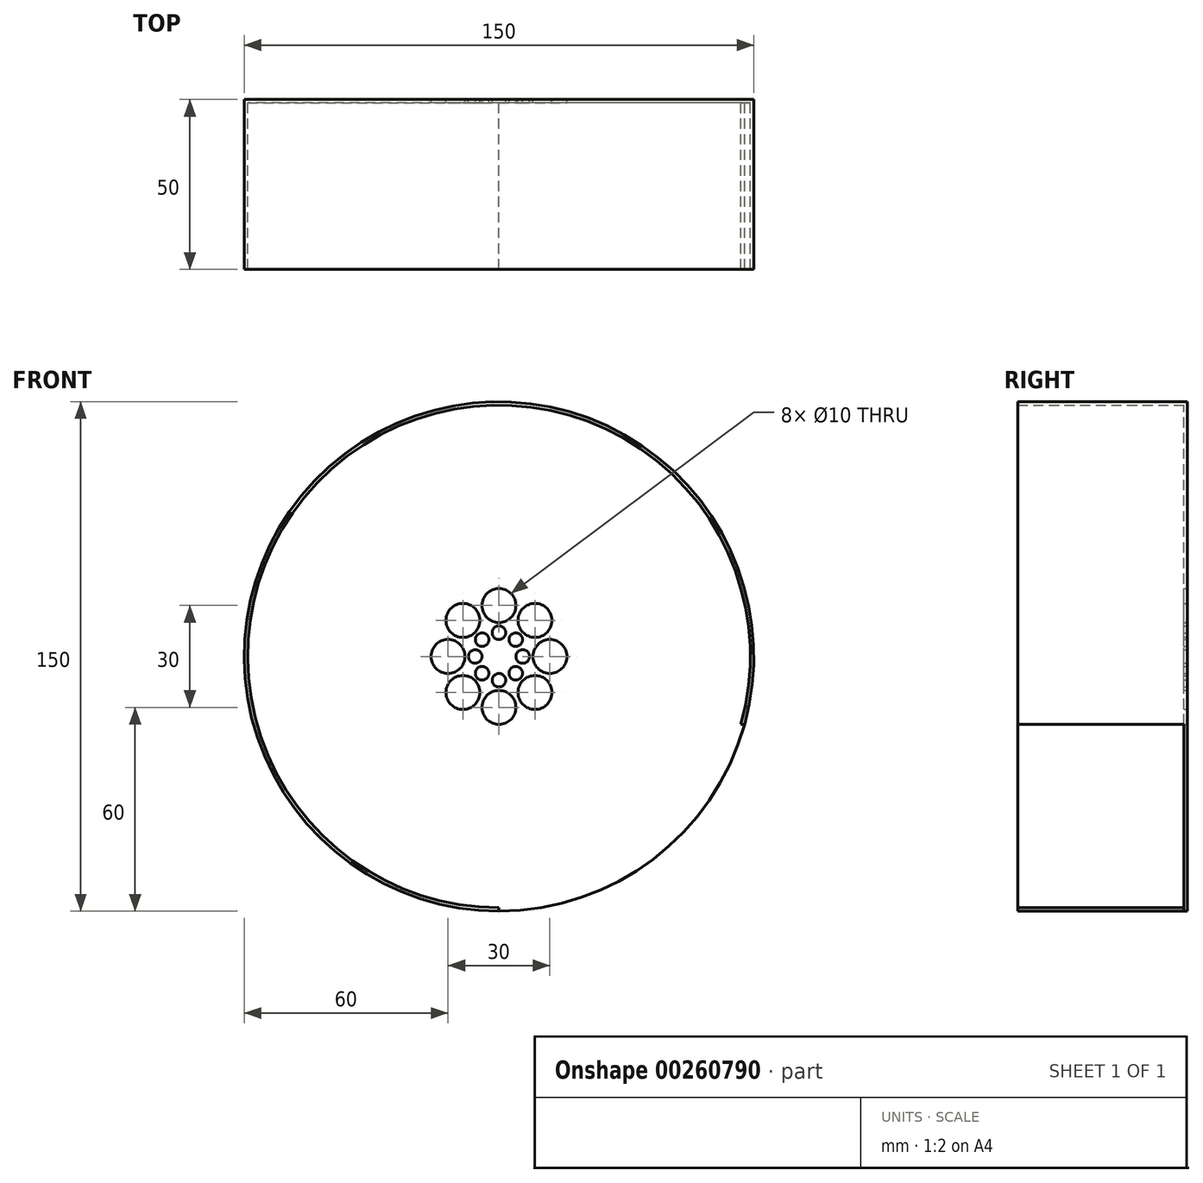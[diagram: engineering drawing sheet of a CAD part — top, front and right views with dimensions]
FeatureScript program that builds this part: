
annotation { "Feature Type Name" : "Feature", "Feature Type Description" : "" }
export const myFeature = defineFeature(function(context is Context, id is Id, definition is map)
    precondition{}
    {
        {
            var Q0;
            Q0=qCreatedBy(makeId("Front.planeOp"),FACE);
            var sketch = newSketch(context, id + "F0", { "sketchPlane" : qUnion([Q0])});
            skCircle(sketch, "E0", {"center": v(0, 0) * mm, "radius": 75 * mm});
            skSolve(sketch);
        }
        {
            var Q0;
            Q0=makeQuery(id+"F0.imprint","IMPRINT",FACE,{"disambiguationData":[TD([[makeQuery(id+"F0.imprint","IMPRINT",EDGE,{"derivedFrom":sQuery(id+"F0.wireOp",EDGE,"E0")}),1.0]])]});
            extrude(context, id + "F1", {"entities" : qUnion([Q0]), "depth" : 50 * mm});
        }
        {
            var Q0;
            Q0=makeQuery(id+"F1.opExtrude","CAP_FACE",FACE,{"disambiguationData":[OSD([sQuery(id+"F0.wireOp",EDGE,"E0")])],"isStart":false});
            shell(context, id + "F2", {"entities" : qUnion([Q0]), "thickness" : 1 * mm});
        }
        {
            var Q0;
            Q0=qCreatedBy(makeId("Right.planeOp"),FACE);
            var sketch = newSketch(context, id + "F3", { "sketchPlane" : qUnion([Q0])});
            skLineSegment(sketch, "E1.bottom", {"start": v(-50, -20) * mm, "end": v(-1, -20) * mm});
            skLineSegment(sketch, "E1.top", {"start": v(-50, -75) * mm, "end": v(-1, -75) * mm});
            skLineSegment(sketch, "E1.left", {"start": v(-50, -20) * mm, "end": v(-50, -75) * mm});
            skLineSegment(sketch, "E1.right", {"start": v(-1, -20) * mm, "end": v(-1, -75) * mm});
            skSolve(sketch);
        }
        {
            var Q0;
            Q0 = qSketchRegion(id + "F3", true);
            extrude(context, id + "F4", {"entities" : qUnion([Q0]), "operationType" : NewBodyOperationType.REMOVE, "depth" : 100 * mm});
        }
        {
            var Q0;
            Q0=makeQuery(id+"F1.opExtrude","CAP_FACE",FACE,{"disambiguationData":[OSD([sQuery(id+"F0.wireOp",EDGE,"E0")])],"isStart":true});
            var sketch = newSketch(context, id + "F5", { "sketchPlane" : qUnion([Q0])});
            skCircle(sketch, "E2", {"center": v(0, 15) * mm, "radius": 5 * mm});
            skCircle(sketch, "E3.1.0", {"center": v(-10.6, 10.6) * mm, "radius": 5 * mm});
            skCircle(sketch, "E3.2.0", {"center": v(-15, 0) * mm, "radius": 5 * mm});
            skCircle(sketch, "E3.3.0", {"center": v(-10.6, -10.6) * mm, "radius": 5 * mm});
            skCircle(sketch, "E3.4.0", {"center": v(0, -15) * mm, "radius": 5 * mm});
            skCircle(sketch, "E3.5.0", {"center": v(10.6, -10.6) * mm, "radius": 5 * mm});
            skCircle(sketch, "E3.6.0", {"center": v(15, 0) * mm, "radius": 5 * mm});
            skCircle(sketch, "E3.7.0", {"center": v(10.6, 10.6) * mm, "radius": 5 * mm});
            skPoint(sketch, "E3.center", {"position": v(0, 0) * mm});
            skCircle(sketch, "E4", {"center": v(0, 7) * mm, "radius": 2 * mm});
            skCircle(sketch, "E5.1.0", {"center": v(-4.95, 4.95) * mm, "radius": 2 * mm});
            skCircle(sketch, "E5.2.0", {"center": v(-7, 0) * mm, "radius": 2 * mm});
            skCircle(sketch, "E5.3.0", {"center": v(-4.95, -4.95) * mm, "radius": 2 * mm});
            skCircle(sketch, "E5.4.0", {"center": v(0, -7) * mm, "radius": 2 * mm});
            skCircle(sketch, "E5.5.0", {"center": v(4.95, -4.95) * mm, "radius": 2 * mm});
            skCircle(sketch, "E5.6.0", {"center": v(7, 0) * mm, "radius": 2 * mm});
            skCircle(sketch, "E5.7.0", {"center": v(4.95, 4.95) * mm, "radius": 2 * mm});
            skSolve(sketch);
        }
        {
            var Q0;
            Q0 = qSketchRegion(id + "F5", true);
            extrude(context, id + "F6", {"entities" : qUnion([Q0]), "operationType" : NewBodyOperationType.REMOVE, "oppositeDirection" : true, "depth" : 25 * mm});
        }
    });
